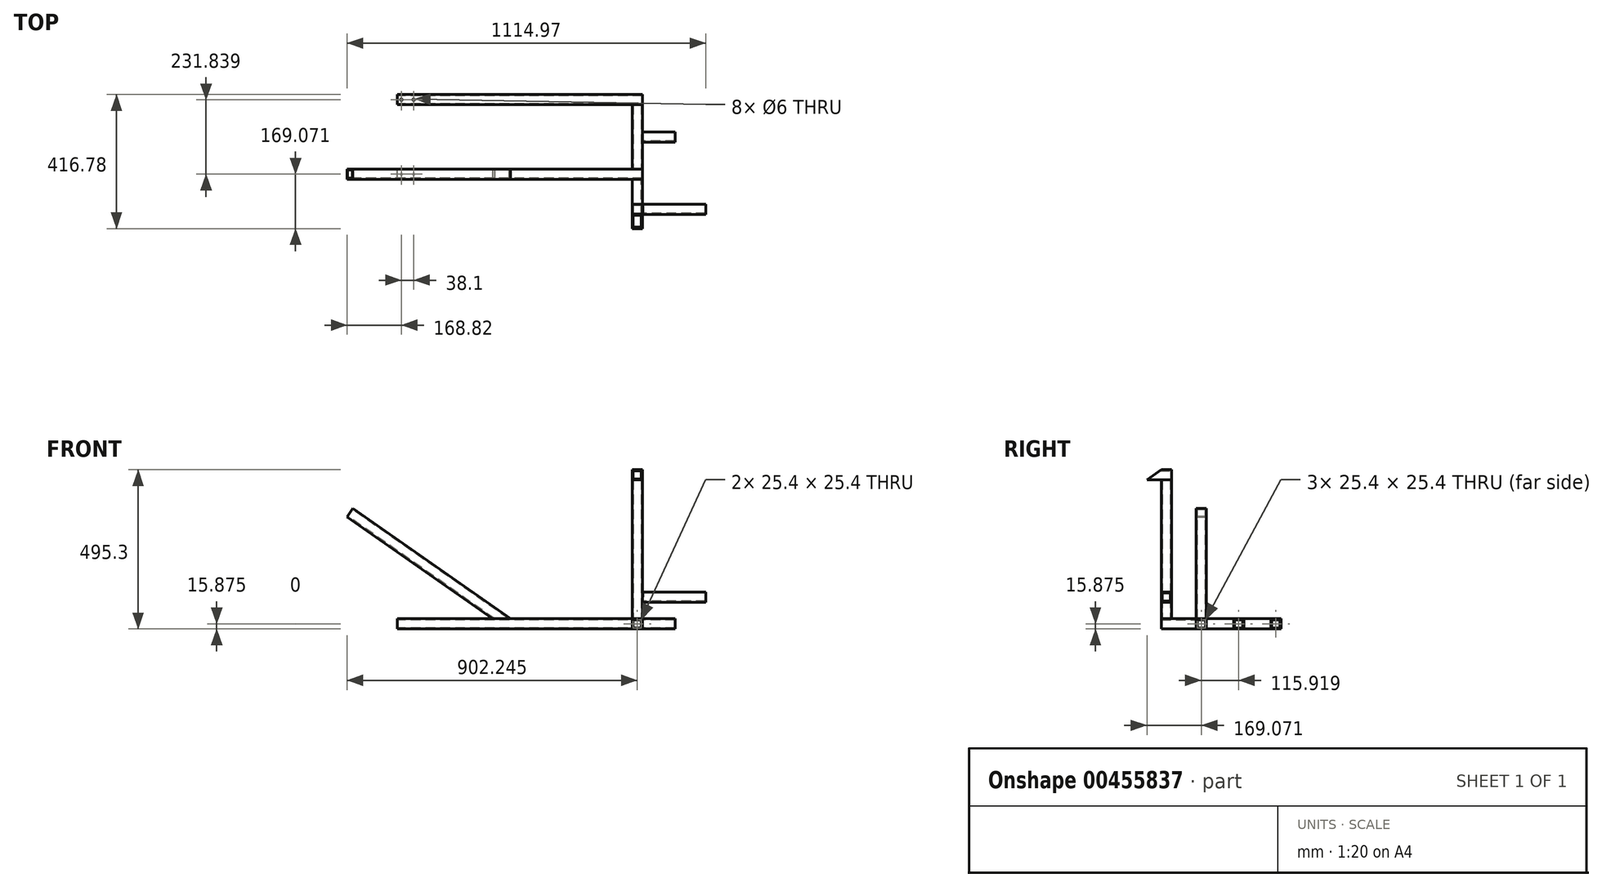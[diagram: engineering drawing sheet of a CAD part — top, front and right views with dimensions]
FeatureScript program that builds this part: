
annotation { "Feature Type Name" : "Feature", "Feature Type Description" : "" }
export const myFeature = defineFeature(function(context is Context, id is Id, definition is map)
    precondition{}
    {
        {
            var Q0;
            Q0=qCreatedBy(makeId("Right.planeOp"),FACE);
            var sketch = newSketch(context, id + "F0", { "sketchPlane" : qUnion([Q0])});
            skLineSegment(sketch, "E0.bottom", {"start": v(-131.8, 0) * mm, "end": v(-100.04, 0) * mm});
            skLineSegment(sketch, "E0.top", {"start": v(-131.8, 31.75) * mm, "end": v(-100.04, 31.75) * mm});
            skLineSegment(sketch, "E0.left", {"start": v(-131.8, 0) * mm, "end": v(-131.8, 31.75) * mm});
            skLineSegment(sketch, "E0.right", {"start": v(-100.04, 0) * mm, "end": v(-100.04, 31.75) * mm});
            skLineSegment(sketch, "E1.0", {"start": v(-128.62, 3.18) * mm, "end": v(-128.62, 28.57) * mm});
            skLineSegment(sketch, "E1.1", {"start": v(-128.62, 3.17) * mm, "end": v(-103.22, 3.17) * mm});
            skLineSegment(sketch, "E1.2", {"start": v(-103.22, 3.18) * mm, "end": v(-103.22, 28.57) * mm});
            skLineSegment(sketch, "E1.3", {"start": v(-128.62, 28.58) * mm, "end": v(-103.22, 28.58) * mm});
            skPoint(sketch, "E2", {"position": v(-115.92, 31.75) * mm});
            skSolve(sketch);
        }
        {
            var Q0;
            Q0=makeQuery(id+"F0.imprint","IMPRINT",FACE,{"disambiguationData":[TD([[makeQuery(id+"F0.imprint","IMPRINT",EDGE,{"derivedFrom":sQuery(id+"F0.wireOp",EDGE,"E0.bottom")}),1.0]])]});
            extrude(context, id + "F1", {"entities" : qUnion([Q0]), "depth" : 762 * mm, "offsetDistance" : 25.4 * mm});
        }
        {
            var Q0;
            Q0=qCreatedBy(makeId("Top.planeOp"),FACE);
            var sketch = newSketch(context, id + "F2", { "sketchPlane" : qUnion([Q0])});
            skCircle(sketch, "E3", {"center": v(12.7, -115.92) * mm, "radius": 3 * mm});
            skCircle(sketch, "E4", {"center": v(50.8, -115.92) * mm, "radius": 3 * mm});
            skSolve(sketch);
        }
        {
            var Q0;
            Q0 = qSketchRegion(id + "F2", true);
            extrude(context, id + "F3", {"entities" : qUnion([Q0]), "operationType" : NewBodyOperationType.REMOVE, "endBound" : BoundingType.THROUGH_ALL, "depth" : 70.61 * mm, "offsetDistance" : 25.4 * mm});
        }
        {
            var Q0;
            Q0=makeQuery(id+"F1.opExtrude","SWEPT_BODY",BODY,{"disambiguationData":[OSD([sQuery(id+"F0.wireOp",EDGE,"E0.bottom"),sQuery(id+"F0.wireOp",EDGE,"E0.top"),sQuery(id+"F0.wireOp",EDGE,"E0.left"),sQuery(id+"F0.wireOp",EDGE,"E0.right"),sQuery(id+"F0.wireOp",EDGE,"E1.0"),sQuery(id+"F0.wireOp",EDGE,"E1.1"),sQuery(id+"F0.wireOp",EDGE,"E1.2"),sQuery(id+"F0.wireOp",EDGE,"E1.3")])]});
            var Q1;
            Q1=qCreatedBy(makeId("Front.planeOp"),FACE);
            mirror(context, id + "F4", {"entities" : qUnion([Q0]), "mirrorPlane" : qUnion([Q1])});
        }
        {
            var Q0;
            Q0=makeQuery(id+"F1.opExtrude","SWEPT_FACE",FACE,{"disambiguationData":[OSD([sQuery(id+"F0.wireOp",EDGE,"E0.right")])]});
            var sketch = newSketch(context, id + "F5", { "sketchPlane" : qUnion([Q0])});
            skLineSegment(sketch, "E5.bottom", {"start": v(-762, 0) * mm, "end": v(-730.25, 0) * mm});
            skLineSegment(sketch, "E5.top", {"start": v(-762, 31.75) * mm, "end": v(-730.25, 31.75) * mm});
            skLineSegment(sketch, "E5.left", {"start": v(-762, 0) * mm, "end": v(-762, 31.75) * mm});
            skLineSegment(sketch, "E5.right", {"start": v(-730.25, 0) * mm, "end": v(-730.25, 31.75) * mm});
            skLineSegment(sketch, "E6.0", {"start": v(-758.83, 28.58) * mm, "end": v(-733.43, 28.58) * mm});
            skLineSegment(sketch, "E6.1", {"start": v(-758.83, 3.18) * mm, "end": v(-758.83, 28.58) * mm});
            skLineSegment(sketch, "E6.2", {"start": v(-758.83, 3.18) * mm, "end": v(-733.43, 3.18) * mm});
            skLineSegment(sketch, "E6.3", {"start": v(-733.43, 3.18) * mm, "end": v(-733.43, 28.58) * mm});
            skSolve(sketch);
        }
        {
            var Q0;
            Q0 = qSketchRegion(id + "F5", true);
            extrude(context, id + "F6", {"entities" : qUnion([Q0]), "endBound" : BoundingType.UP_TO_NEXT, "depth" : 25.4 * mm, "offsetDistance" : 25.4 * mm});
        }
        {
            var Q0;
            Q0=makeQuery(id+"F6.opExtrude","SWEPT_FACE",FACE,{"disambiguationData":[OSD([sQuery(id+"F5.wireOp",EDGE,"E5.left")])]});
            var sketch = newSketch(context, id + "F7", { "sketchPlane" : qUnion([Q0])});
            skLineSegment(sketch, "E7.bottom", {"start": v(-15.88, 0) * mm, "end": v(15.88, 0) * mm});
            skLineSegment(sketch, "E7.top", {"start": v(-15.88, 31.75) * mm, "end": v(15.87, 31.75) * mm});
            skLineSegment(sketch, "E7.left", {"start": v(-15.88, 0) * mm, "end": v(-15.88, 31.75) * mm});
            skLineSegment(sketch, "E7.right", {"start": v(15.88, 0) * mm, "end": v(15.87, 31.75) * mm});
            skLineSegment(sketch, "E8.0", {"start": v(-12.7, 3.18) * mm, "end": v(-12.7, 28.58) * mm});
            skLineSegment(sketch, "E8.1", {"start": v(-12.7, 3.18) * mm, "end": v(12.7, 3.18) * mm});
            skLineSegment(sketch, "E8.2", {"start": v(12.7, 3.18) * mm, "end": v(12.7, 28.58) * mm});
            skLineSegment(sketch, "E8.3", {"start": v(-12.7, 28.58) * mm, "end": v(12.7, 28.58) * mm});
            skSolve(sketch);
        }
        {
            var Q0;
            Q0 = qSketchRegion(id + "F7", true);
            extrude(context, id + "F8", {"entities" : qUnion([Q0]), "depth" : 101.6 * mm, "offsetDistance" : 25.4 * mm});
        }
        {
            var Q0;
            Q0=makeQuery(id+"F1.opExtrude","SWEPT_FACE",FACE,{"disambiguationData":[OSD([sQuery(id+"F0.wireOp",EDGE,"E0.left")])]});
            var sketch = newSketch(context, id + "F9", { "sketchPlane" : qUnion([Q0])});
            skLineSegment(sketch, "E9.0", {"start": v(758.83, 28.58) * mm, "end": v(733.43, 28.58) * mm});
            skLineSegment(sketch, "E9.1", {"start": v(733.43, 3.18) * mm, "end": v(733.43, 28.58) * mm});
            skLineSegment(sketch, "E9.2", {"start": v(758.83, 3.18) * mm, "end": v(733.43, 3.18) * mm});
            skLineSegment(sketch, "E9.3", {"start": v(762, 0) * mm, "end": v(730.25, 0) * mm});
            skLineSegment(sketch, "E9.4", {"start": v(730.25, 0) * mm, "end": v(730.25, 31.75) * mm});
            skLineSegment(sketch, "E9.5", {"start": v(762, 31.75) * mm, "end": v(730.25, 31.75) * mm});
            skLineSegment(sketch, "E9.6", {"start": v(762, 0) * mm, "end": v(762, 31.75) * mm});
            skLineSegment(sketch, "E9.7", {"start": v(758.83, 3.18) * mm, "end": v(758.83, 28.58) * mm});
            skSolve(sketch);
        }
        {
            var Q0;
            Q0 = qSketchRegion(id + "F9", true);
            extrude(context, id + "F10", {"entities" : qUnion([Q0]), "depth" : 108.74 * mm, "offsetDistance" : 25.4 * mm});
        }
        {
            var Q0;
            Q0=makeQuery(id+"F10.opExtrude","SWEPT_FACE",FACE,{"disambiguationData":[OSD([sQuery(id+"F9.wireOp",EDGE,"E9.5")])]});
            var sketch = newSketch(context, id + "F11", { "sketchPlane" : qUnion([Q0])});
            skLineSegment(sketch, "E10.bottom", {"start": v(762, -240.54) * mm, "end": v(730.25, -240.54) * mm});
            skLineSegment(sketch, "E10.top", {"start": v(762, -208.79) * mm, "end": v(730.25, -208.79) * mm});
            skLineSegment(sketch, "E10.left", {"start": v(762, -240.54) * mm, "end": v(762, -208.79) * mm});
            skLineSegment(sketch, "E10.right", {"start": v(730.25, -240.54) * mm, "end": v(730.25, -208.79) * mm});
            skLineSegment(sketch, "E11.0", {"start": v(758.83, -211.96) * mm, "end": v(733.43, -211.96) * mm});
            skLineSegment(sketch, "E11.1", {"start": v(758.83, -237.36) * mm, "end": v(758.83, -211.96) * mm});
            skLineSegment(sketch, "E11.2", {"start": v(758.83, -237.36) * mm, "end": v(733.43, -237.36) * mm});
            skLineSegment(sketch, "E11.3", {"start": v(733.43, -237.36) * mm, "end": v(733.43, -211.96) * mm});
            skSolve(sketch);
        }
        {
            var Q0;
            Q0 = qSketchRegion(id + "F11", true);
            extrude(context, id + "F12", {"entities" : qUnion([Q0]), "depth" : 431.8 * mm, "offsetDistance" : 25.4 * mm});
        }
        {
            var Q0;
            Q0=makeQuery(id+"F12.opExtrude","SWEPT_FACE",FACE,{"disambiguationData":[OSD([sQuery(id+"F11.wireOp",EDGE,"E10.bottom")])]});
            var sketch = newSketch(context, id + "F13", { "sketchPlane" : qUnion([Q0])});
            skLineSegment(sketch, "E12", {"start": v(762, 31.75) * mm, "end": v(730.25, 31.75) * mm});
            skLineSegment(sketch, "E13", {"start": v(730.25, 31.75) * mm, "end": v(730.25, 33.14) * mm});
            skLineSegment(sketch, "E14", {"start": v(730.25, 33.14) * mm, "end": v(762, 31.75) * mm});
            skSolve(sketch);
        }
        {
            var Q0;
            Q0 = qSketchRegion(id + "F13", true);
            extrude(context, id + "F14", {"entities" : qUnion([Q0]), "operationType" : NewBodyOperationType.REMOVE, "oppositeDirection" : true, "depth" : 60.7 * mm, "offsetDistance" : 25.4 * mm});
        }
        {
            var Q0;
            Q0=makeQuery(id+"F12.opExtrude","SWEPT_FACE",FACE,{"disambiguationData":[OSD([sQuery(id+"F11.wireOp",EDGE,"E10.top")])]});
            var sketch = newSketch(context, id + "F15", { "sketchPlane" : qUnion([Q0])});
            skLineSegment(sketch, "E15.bottom", {"start": v(-762, 463.55) * mm, "end": v(-730.25, 463.55) * mm});
            skLineSegment(sketch, "E15.top", {"start": v(-762, 495.3) * mm, "end": v(-730.25, 495.3) * mm});
            skLineSegment(sketch, "E15.left", {"start": v(-762, 463.55) * mm, "end": v(-762, 495.3) * mm});
            skLineSegment(sketch, "E15.right", {"start": v(-730.25, 463.55) * mm, "end": v(-730.25, 495.3) * mm});
            skLineSegment(sketch, "E16.0", {"start": v(-758.83, 466.73) * mm, "end": v(-758.83, 492.13) * mm});
            skLineSegment(sketch, "E16.1", {"start": v(-758.83, 466.73) * mm, "end": v(-733.43, 466.73) * mm});
            skLineSegment(sketch, "E16.2", {"start": v(-733.43, 466.73) * mm, "end": v(-733.43, 492.13) * mm});
            skLineSegment(sketch, "E16.3", {"start": v(-758.83, 492.13) * mm, "end": v(-733.43, 492.13) * mm});
            skSolve(sketch);
        }
        {
            var Q0;
            Q0 = qSketchRegion(id + "F15", true);
            extrude(context, id + "F16", {"entities" : qUnion([Q0]), "oppositeDirection" : true, "depth" : 76.2 * mm, "offsetDistance" : 25.4 * mm});
        }
        {
            var Q0;
            Q0=makeQuery(id+"F16.opExtrude","SWEPT_FACE",FACE,{"disambiguationData":[OSD([sQuery(id+"F15.wireOp",EDGE,"E15.right")])]});
            var sketch = newSketch(context, id + "F17", { "sketchPlane" : qUnion([Q0])});
            skLineSegment(sketch, "E17", {"start": v(284.99, 463.55) * mm, "end": v(239.64, 495.3) * mm});
            skLineSegment(sketch, "E18", {"start": v(239.64, 495.3) * mm, "end": v(284.99, 495.3) * mm});
            skLineSegment(sketch, "E19", {"start": v(284.99, 495.3) * mm, "end": v(284.99, 463.55) * mm});
            skSolve(sketch);
        }
        {
            var Q0;
            Q0 = qSketchRegion(id + "F17", true);
            extrude(context, id + "F18", {"entities" : qUnion([Q0]), "operationType" : NewBodyOperationType.REMOVE, "endBound" : BoundingType.THROUGH_ALL, "oppositeDirection" : true, "depth" : 25.4 * mm, "offsetDistance" : 25.4 * mm});
        }
        {
            var Q0;
            Q0=makeQuery(id+"F1.opExtrude","SWEPT_FACE",FACE,{"disambiguationData":[OSD([sQuery(id+"F0.wireOp",EDGE,"E0.left")])]});
            var sketch = newSketch(context, id + "F19", { "sketchPlane" : qUnion([Q0])});
            skPoint(sketch, "E20", {"position": v(-170.69, 327.91) * mm});
            skLineSegment(sketch, "E21", {"start": v(-170.69, 327.91) * mm, "end": v(252.28, 31.75) * mm});
            skLineSegment(sketch, "E22.0", {"start": v(-156.12, 348.72) * mm, "end": v(266.85, 52.56) * mm});
            skSolve(sketch);
        }
        {
            var Q0;
            Q0=makeQuery(id+"F12.opExtrude","SWEPT_FACE",FACE,{"disambiguationData":[OSD([sQuery(id+"F11.wireOp",EDGE,"E10.left")])]});
            var sketch = newSketch(context, id + "F20", { "sketchPlane" : qUnion([Q0])});
            skLineSegment(sketch, "E23.bottom", {"start": v(-240.54, 82.87) * mm, "end": v(-208.79, 82.87) * mm});
            skLineSegment(sketch, "E23.top", {"start": v(-240.54, 114.62) * mm, "end": v(-208.79, 114.62) * mm});
            skLineSegment(sketch, "E23.left", {"start": v(-240.54, 82.87) * mm, "end": v(-240.54, 114.62) * mm});
            skLineSegment(sketch, "E23.right", {"start": v(-208.79, 82.87) * mm, "end": v(-208.79, 114.62) * mm});
            skLineSegment(sketch, "E24.0", {"start": v(-237.36, 86.04) * mm, "end": v(-237.36, 111.44) * mm});
            skLineSegment(sketch, "E24.1", {"start": v(-237.36, 86.04) * mm, "end": v(-211.96, 86.04) * mm});
            skLineSegment(sketch, "E24.2", {"start": v(-211.96, 86.04) * mm, "end": v(-211.96, 111.44) * mm});
            skLineSegment(sketch, "E24.3", {"start": v(-237.36, 111.44) * mm, "end": v(-211.96, 111.44) * mm});
            skSolve(sketch);
        }
        {
            var Q0;
            Q0 = qSketchRegion(id + "F20", true);
            extrude(context, id + "F21", {"entities" : qUnion([Q0]), "depth" : 196.85 * mm, "offsetDistance" : 25.4 * mm});
        }
        {
            var Q0;
            Q0=makeQuery(id+"F21.opExtrude","SWEPT_FACE",FACE,{"disambiguationData":[OSD([sQuery(id+"F20.wireOp",EDGE,"E23.left")])]});
            var sketch = newSketch(context, id + "F22", { "sketchPlane" : qUnion([Q0])});
            skLineSegment(sketch, "E25", {"start": v(762, 82.87) * mm, "end": v(763.39, 114.62) * mm});
            skLineSegment(sketch, "E26", {"start": v(763.39, 114.62) * mm, "end": v(762, 114.62) * mm});
            skLineSegment(sketch, "E27", {"start": v(762, 114.62) * mm, "end": v(762, 82.87) * mm});
            skSolve(sketch);
        }
        {
            var Q0;
            Q0 = qSketchRegion(id + "F22", true);
            extrude(context, id + "F23", {"entities" : qUnion([Q0]), "operationType" : NewBodyOperationType.REMOVE, "oppositeDirection" : true, "depth" : 41.4 * mm, "offsetDistance" : 25.4 * mm});
        }
        {
            var Q0;
            Q0=sQuery(id+"F19.wireOp",EDGE,"E22.0");
            var Q1;
            Q1=sQuery(id+"F19.wireOp",VERTEX,"E22.0.start");
            cPlane(context, id + "F24", {"entities" : qUnion([Q0, Q1]), "cplaneType" : CPlaneType.LINE_POINT, "offset" : 25.4 * mm, "width" : 152.4 * mm, "height" : 152.4 * mm});
        }
        {
            var Q0;
            Q0=qCreatedBy(id+"F24.planeOp",FACE);
            var sketch = newSketch(context, id + "F25", { "sketchPlane" : qUnion([Q0])});
            skLineSegment(sketch, "E28.bottom", {"start": v(-131.8, 196.1) * mm, "end": v(-100.04, 196.1) * mm});
            skLineSegment(sketch, "E28.top", {"start": v(-131.8, 227.86) * mm, "end": v(-100.04, 227.86) * mm});
            skLineSegment(sketch, "E28.left", {"start": v(-131.8, 196.1) * mm, "end": v(-131.8, 227.86) * mm});
            skLineSegment(sketch, "E28.right", {"start": v(-100.04, 196.1) * mm, "end": v(-100.04, 227.86) * mm});
            skLineSegment(sketch, "E29.0", {"start": v(-128.62, 199.28) * mm, "end": v(-103.22, 199.28) * mm});
            skLineSegment(sketch, "E29.1", {"start": v(-128.62, 199.28) * mm, "end": v(-128.62, 224.68) * mm});
            skLineSegment(sketch, "E29.2", {"start": v(-128.62, 224.68) * mm, "end": v(-103.22, 224.68) * mm});
            skLineSegment(sketch, "E29.3", {"start": v(-103.22, 199.28) * mm, "end": v(-103.22, 224.68) * mm});
            skSolve(sketch);
        }
        {
            var Q0;
            Q0 = qSketchRegion(id + "F25", true);
            extrude(context, id + "F26", {"entities" : qUnion([Q0]), "endBound" : BoundingType.UP_TO_NEXT, "depth" : 25.4 * mm, "offsetDistance" : 25.4 * mm});
        }
    });
